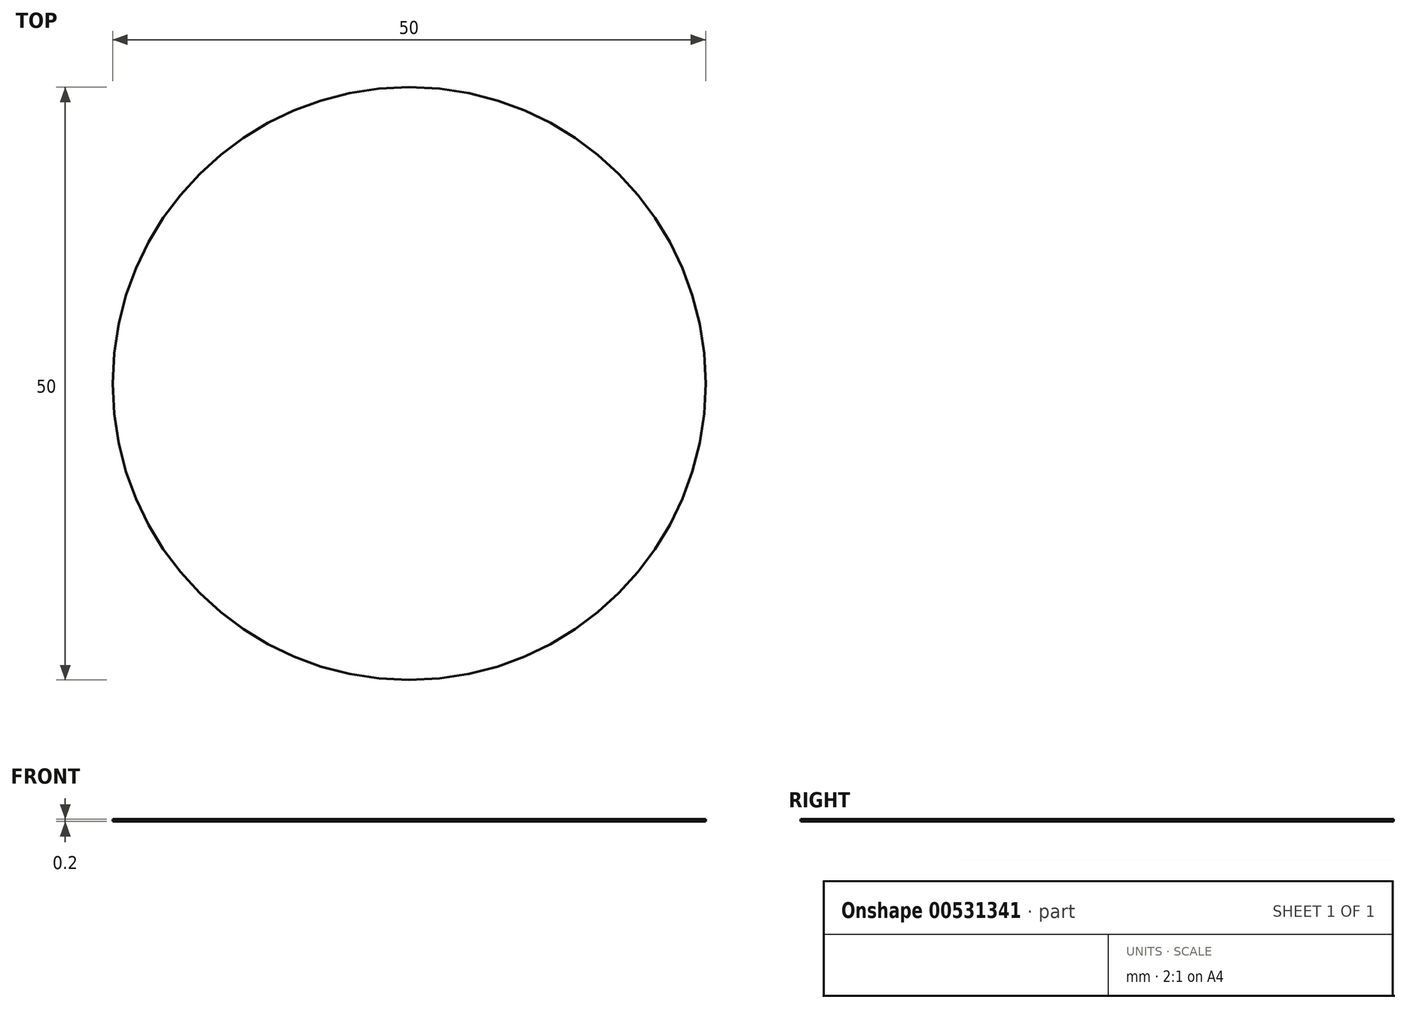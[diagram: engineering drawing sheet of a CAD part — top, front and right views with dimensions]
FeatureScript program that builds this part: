
annotation { "Feature Type Name" : "Feature", "Feature Type Description" : "" }
export const myFeature = defineFeature(function(context is Context, id is Id, definition is map)
    precondition{}
    {
        {
            var Q0;
            Q0=qCreatedBy(makeId("Top.planeOp"),FACE);
            var sketch = newSketch(context, id + "F0", { "sketchPlane" : qUnion([Q0])});
            skCircle(sketch, "E0", {"center": v(0, 0) * mm, "radius": 25 * mm});
            skSolve(sketch);
        }
        {
            var Q0;
            Q0=makeQuery(id+"F0.imprint","IMPRINT",FACE,{"disambiguationData":[TD([[makeQuery(id+"F0.imprint","IMPRINT",EDGE,{"derivedFrom":sQuery(id+"F0.wireOp",EDGE,"E0")}),1.0]])]});
            extrude(context, id + "F1", {"entities" : qUnion([Q0]), "depth" : .2 * mm, "offsetDistance" : 25.4 * mm});
        }
    });
